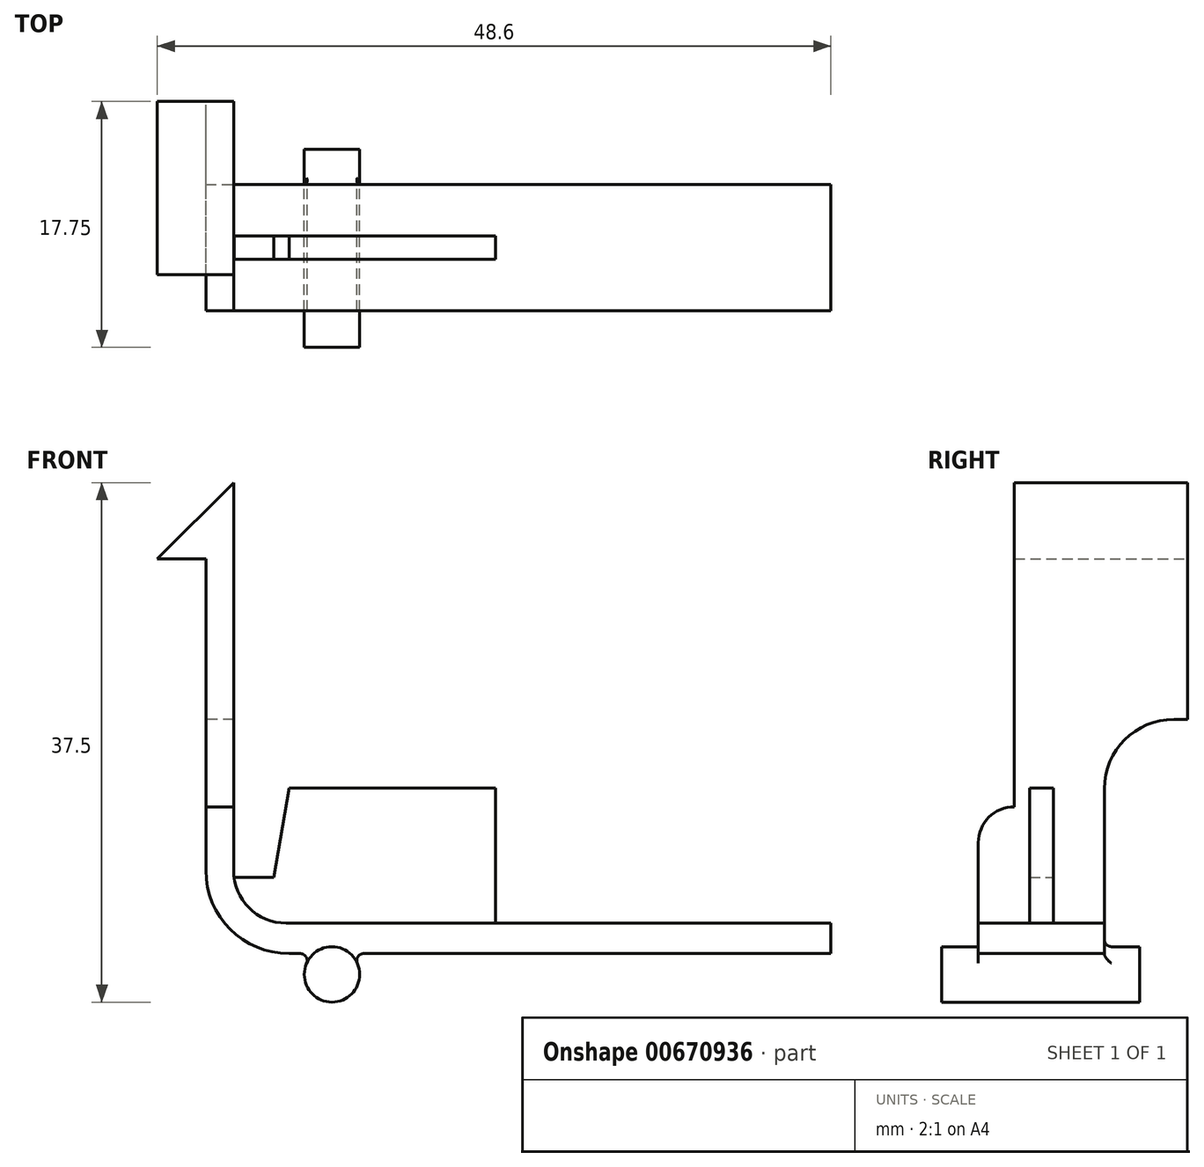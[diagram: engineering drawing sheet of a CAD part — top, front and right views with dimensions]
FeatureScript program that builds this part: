
annotation { "Feature Type Name" : "Feature", "Feature Type Description" : "" }
export const myFeature = defineFeature(function(context is Context, id is Id, definition is map)
    precondition{}
    {
        {
            var Q0;
            Q0=qCreatedBy(makeId("Front.planeOp"),FACE);
            var sketch = newSketch(context, id + "F0", { "sketchPlane" : qUnion([Q0])});
            skLineSegment(sketch, "E0", {"start": v(45.1, 3.5) * mm, "end": v(6, 3.5) * mm});
            skLineSegment(sketch, "E1", {"start": v(0, 9.5) * mm, "end": v(0, 32) * mm});
            skLineSegment(sketch, "E2", {"start": v(2, 37.5) * mm, "end": v(2, 9.5) * mm});
            skLineSegment(sketch, "E3", {"start": v(5.8, 5.7) * mm, "end": v(45.1, 5.7) * mm});
            skLineSegment(sketch, "E4", {"start": v(45.1, 3.5) * mm, "end": v(45.1, 5.7) * mm});
            skCircle(sketch, "E5", {"center": v(9.1, 2) * mm, "radius": 2 * mm});
            skPoint(sketch, "E6.visualSharp", {"position": v(0, 3.5) * mm});
            skArc(sketch, "E6.filletArc", {"start": v(0, 9.5) * mm, "mid": v(1.76, 5.26) * mm, "end": v(6, 3.5) * mm});
            skPoint(sketch, "E7.visualSharp", {"position": v(2, 5.7) * mm});
            skArc(sketch, "E7.filletArc", {"start": v(2, 9.5) * mm, "mid": v(3.11, 6.81) * mm, "end": v(5.8, 5.7) * mm});
            skLineSegment(sketch, "E8", {"start": v(2, 37.5) * mm, "end": v(-3.5, 32) * mm});
            skLineSegment(sketch, "E9", {"start": v(-3.5, 32) * mm, "end": v(0, 32) * mm});
            skSolve(sketch);
        }
        {
            var Q0;
            Q0=makeQuery(id+"F0.imprint","IMPRINT",FACE,{"disambiguationData":[TD([[makeQuery(id+"F0.imprint","IMPRINT",EDGE,{"derivedFrom":sQuery(id+"F0.wireOp",EDGE,"E1")}),-1.0]])]});
            extrude(context, id + "F1", {"entities" : qUnion([Q0]), "endBound" : BoundingType.SYMMETRIC, "depth" : 9.1 * mm, "offsetDistance" : 25 * mm});
        }
        {
            var Q0;
            {var subQ0=sQuery(id+"F0.wireOp",EDGE,"E5");var subQ1=sQuery(id+"F0.wireOp",EDGE,"E0");var subQ2=makeQuery(id+"F0.imprint","INTERSECT",VERTEX,{"disambiguationData":[OD(0.0)],"derivedFrom":[subQ1,subQ0]});Q0=makeQuery(id+"F0.imprint","IMPRINT",FACE,{"disambiguationData":[TD([[makeQuery(id+"F0.imprint","IMPRINT",EDGE,{"disambiguationData":[TD([[subQ2,-1.0]])],"derivedFrom":subQ1}),1.0]])]});}
            var Q1;
            {var subQ0=sQuery(id+"F0.wireOp",EDGE,"E5");var subQ1=sQuery(id+"F0.wireOp",EDGE,"E0");var subQ2=makeQuery(id+"F0.imprint","INTERSECT",VERTEX,{"disambiguationData":[OD(0.0)],"derivedFrom":[subQ1,subQ0]});Q1=makeQuery(id+"F0.imprint","IMPRINT",FACE,{"disambiguationData":[TD([[makeQuery(id+"F0.imprint","IMPRINT",EDGE,{"disambiguationData":[TD([[subQ2,-1.0]])],"derivedFrom":subQ1}),-1.0]])]});}
            extrude(context, id + "F2", {"entities" : qUnion([Q0, Q1]), "operationType" : NewBodyOperationType.ADD, "depth" : (2.6 + 9.2 / 2) * mm, "offsetDistance" : 25 * mm});
        }
        {
            var Q0;
            Q0=makeQuery(id+"F2.opExtrude","CAP_FACE",FACE,{"disambiguationData":[OSD([sQuery(id+"F0.wireOp",EDGE,"E5")])],"isStart":false});
            extrude(context, id + "F3", {"entities" : qUnion([Q0]), "operationType" : NewBodyOperationType.ADD, "oppositeDirection" : true, "depth" : 14.3 * mm, "offsetDistance" : 25 * mm});
        }
        {
            var Q0;
            Q0=qCreatedBy(makeId("Front.planeOp"),FACE);
            var sketch = newSketch(context, id + "F4", { "sketchPlane" : qUnion([Q0])});
            skLineSegment(sketch, "E10", {"start": v(20.9, 15.45) * mm, "end": v(6, 15.45) * mm});
            skLineSegment(sketch, "E11", {"start": v(6, 15.45) * mm, "end": v(4.9, 9) * mm});
            skLineSegment(sketch, "E12", {"start": v(4.9, 9) * mm, "end": v(2, 9) * mm});
            skLineSegment(sketch, "E13", {"start": v(20.9, 15.45) * mm, "end": v(20.9, 5.7) * mm});
            skArc(sketch, "E14.0", {"start": v(2.03, 9) * mm, "mid": v(3.3, 6.64) * mm, "end": v(5.8, 5.7) * mm});
            skLineSegment(sketch, "E15.0", {"start": v(5.8, 5.7) * mm, "end": v(20.9, 5.7) * mm});
            skPoint(sketch, "E16.orphan", {"position": v(2, 37.5) * mm});
            skPoint(sketch, "E17.orphan", {"position": v(45.1, 5.7) * mm});
            skPoint(sketch, "E18.orphan", {"position": v(2, 9.5) * mm});
            skSolve(sketch);
        }
        {
            var Q0;
            Q0 = qSketchRegion(id + "F4", true);
            extrude(context, id + "F5", {"entities" : qUnion([Q0]), "operationType" : NewBodyOperationType.ADD, "endBound" : BoundingType.SYMMETRIC, "depth" : 1.7 * mm, "offsetDistance" : 25 * mm});
        }
        {
            var Q0;
            Q0=makeQuery(id+"F1.opExtrude","CAP_FACE",FACE,{"disambiguationData":[OSD([sQuery(id+"F0.wireOp",EDGE,"E0"),sQuery(id+"F0.wireOp",EDGE,"E1"),sQuery(id+"F0.wireOp",EDGE,"E2"),sQuery(id+"F0.wireOp",EDGE,"E3"),sQuery(id+"F0.wireOp",EDGE,"E4"),sQuery(id+"F0.wireOp",EDGE,"E5"),sQuery(id+"F0.wireOp",EDGE,"E6.filletArc"),sQuery(id+"F0.wireOp",EDGE,"E7.filletArc"),sQuery(id+"F0.wireOp",EDGE,"E8"),sQuery(id+"F0.wireOp",EDGE,"E9")])],"isStart":true});
            var sketch = newSketch(context, id + "F6", { "sketchPlane" : qUnion([Q0])});
            skLineSegment(sketch, "E19.0.3", {"start": v(0, 15.4) * mm, "end": v(0, 32) * mm});
            skLineSegment(sketch, "E19.0.4", {"start": v(0, 32) * mm, "end": v(3.5, 32) * mm});
            skLineSegment(sketch, "E19.0.5", {"start": v(3.5, 32) * mm, "end": v(-2, 37.5) * mm});
            skLineSegment(sketch, "E19.0.6", {"start": v(-2, 37.5) * mm, "end": v(-2, 15.4) * mm});
            skLineSegment(sketch, "E20", {"start": v(0, 15.4) * mm, "end": v(-2, 15.4) * mm});
            skPoint(sketch, "E19.0.7.start.orphan", {"position": v(-2, 9.5) * mm});
            skPoint(sketch, "E19.0.2.end.orphan", {"position": v(0, 9.5) * mm});
            skPoint(sketch, "E19.0.8.start.orphan", {"position": v(-5.8, 5.7) * mm});
            skPoint(sketch, "E19.0.1.end.orphan", {"position": v(-6, 3.5) * mm});
            skPoint(sketch, "E19.0.0.end.orphan", {"position": v(-7.78, 3.5) * mm});
            skPoint(sketch, "E19.0.10.end.orphan", {"position": v(-10.42, 3.5) * mm});
            skPoint(sketch, "E19.0.9.end.orphan", {"position": v(-45.1, 3.5) * mm});
            skPoint(sketch, "E19.0.9.start.orphan", {"position": v(-45.1, 5.7) * mm});
            skSolve(sketch);
        }
        {
            var Q0;
            Q0 = qSketchRegion(id + "F6", true);
            extrude(context, id + "F7", {"entities" : qUnion([Q0]), "operationType" : NewBodyOperationType.ADD, "depth" : 6 * mm, "offsetDistance" : 25 * mm});
        }
        {
            var Q0;
            Q0=makeQuery(id+"F7.boolean.opBoolean","MERGE",FACE,{"derivedFrom":[makeQuery(id+"F1.opExtrude","SWEPT_FACE",FACE,{"disambiguationData":[OSD([sQuery(id+"F0.wireOp",EDGE,"E1")])]}),makeQuery(id+"F7.opExtrude","SWEPT_FACE",FACE,{"disambiguationData":[OSD([sQuery(id+"F6.wireOp",EDGE,"E19.0.3")])]})]});
            var sketch = newSketch(context, id + "F8", { "sketchPlane" : qUnion([Q0])});
            skLineSegment(sketch, "E21", {"start": v(-4.55, 37.5) * mm, "end": v(-4.55, 42.04) * mm});
            skLineSegment(sketch, "E22", {"start": v(-4.55, 42.04) * mm, "end": v(-13.48, 42.04) * mm});
            skLineSegment(sketch, "E23", {"start": v(-13.48, 42.04) * mm, "end": v(-13.48, 13.67) * mm});
            skLineSegment(sketch, "E24", {"start": v(-13.48, 13.67) * mm, "end": v(-4.55, 13.67) * mm});
            skLineSegment(sketch, "E25", {"start": v(-4.55, 13.67) * mm, "end": v(-4.55, 15.4) * mm});
            skLineSegment(sketch, "E26", {"start": v(-9.55, 20.4) * mm, "end": v(-10.55, 20.4) * mm});
            skLineSegment(sketch, "E27", {"start": v(-10.55, 20.4) * mm, "end": v(-10.55, 37.5) * mm});
            skLineSegment(sketch, "E28", {"start": v(-10.55, 37.5) * mm, "end": v(-4.55, 37.5) * mm});
            skPoint(sketch, "E29.visualSharp", {"position": v(-4.55, 20.4) * mm});
            skArc(sketch, "E29.filletArc", {"start": v(-4.55, 15.4) * mm, "mid": v(-6.01, 18.94) * mm, "end": v(-9.55, 20.4) * mm});
            skSolve(sketch);
        }
        {
            var Q0;
            Q0=makeQuery(id+"F8.imprint","IMPRINT",FACE,{"disambiguationData":[TD([[makeQuery(id+"F8.imprint","IMPRINT",EDGE,{"derivedFrom":sQuery(id+"F8.wireOp",EDGE,"E21")}),1.0]])]});
            var Q1;
            {var subQ0=sQuery(id+"F8.wireOp",EDGE,"E26");Q1=makeQuery(id+"F8.imprint","IMPRINT",FACE,{"disambiguationData":[TD([[makeQuery(id+"F8.imprint","IMPRINT",EDGE,{"derivedFrom":subQ0}),1.0]])]});}
            extrude(context, id + "F9", {"entities" : qUnion([Q0, Q1]), "operationType" : NewBodyOperationType.REMOVE, "oppositeDirection" : true, "depth" : 3.6 * mm, "offsetDistance" : 25 * mm});
        }
        {
            var Q0;
            Q0=makeQuery(id+"F7.boolean.opBoolean","MERGE",FACE,{"derivedFrom":[makeQuery(id+"F1.opExtrude","SWEPT_FACE",FACE,{"disambiguationData":[OSD([sQuery(id+"F0.wireOp",EDGE,"E1")])]}),makeQuery(id+"F7.opExtrude","SWEPT_FACE",FACE,{"disambiguationData":[OSD([sQuery(id+"F6.wireOp",EDGE,"E19.0.3")])]})]});
            var sketch = newSketch(context, id + "F10", { "sketchPlane" : qUnion([Q0])});
            skLineSegment(sketch, "E30", {"start": v(1.95, 37.5) * mm, "end": v(1.95, 14.1) * mm});
            skArc(sketch, "E31", {"start": v(4.55, 11.5) * mm, "mid": v(3.79, 13.34) * mm, "end": v(1.95, 14.1) * mm});
            skLineSegment(sketch, "E32", {"start": v(4.55, 37.5) * mm, "end": v(4.55, 11.5) * mm});
            skLineSegment(sketch, "E33", {"start": v(4.55, 37.5) * mm, "end": v(1.95, 37.5) * mm});
            skSolve(sketch);
        }
        {
            var Q0;
            Q0 = qSketchRegion(id + "F10", true);
            extrude(context, id + "F11", {"entities" : qUnion([Q0]), "operationType" : NewBodyOperationType.REMOVE, "endBound" : BoundingType.SYMMETRIC, "oppositeDirection" : true, "depth" : 25 * mm, "offsetDistance" : 25 * mm});
        }
        {
            var Q0;
            {var subQ0=sQuery(id+"F0.wireOp",EDGE,"E0");var subQ1=sQuery(id+"F0.wireOp",EDGE,"E5");var subQ2=makeQuery(id+"F0.imprint","INTERSECT",VERTEX,{"disambiguationData":[OD(1.0)],"derivedFrom":[subQ0,subQ1]});var subQ4=makeQuery(id+"F1.opExtrude","SWEPT_EDGE",EDGE,{"disambiguationData":[OSD([subQ0,subQ1]),TDD([subQ2])]});Q0=makeQuery(id+"F3.boolean.opBoolean","MERGE",EDGE,{"derivedFrom":[makeQuery(id+"F2.boolean.opBoolean","SPLIT",EDGE,{"disambiguationData":[topologyDisambiguationEdgeConnected([makeQuery(id+"F1.opExtrude","SWEPT_FACE",FACE,{"disambiguationData":[OSD([subQ1])]})])],"derivedFrom":subQ4}),makeQuery(id+"F2.boolean.opBoolean","SPLIT",EDGE,{"disambiguationData":[topologyDisambiguationEdgeConnected([makeQuery(id+"F2.opExtrude","SWEPT_FACE",FACE,{"disambiguationData":[OSD([subQ1])]})])],"derivedFrom":subQ4})]});}
            var Q1;
            {var subQ0=sQuery(id+"F0.wireOp",EDGE,"E0");var subQ1=sQuery(id+"F0.wireOp",EDGE,"E5");var subQ2=makeQuery(id+"F0.imprint","INTERSECT",VERTEX,{"disambiguationData":[OD(0.0)],"derivedFrom":[subQ0,subQ1]});var subQ4=makeQuery(id+"F1.opExtrude","SWEPT_EDGE",EDGE,{"disambiguationData":[OSD([subQ0,subQ1]),TDD([subQ2])]});Q1=makeQuery(id+"F3.boolean.opBoolean","MERGE",EDGE,{"derivedFrom":[makeQuery(id+"F2.boolean.opBoolean","SPLIT",EDGE,{"disambiguationData":[topologyDisambiguationEdgeConnected([makeQuery(id+"F1.opExtrude","SWEPT_FACE",FACE,{"disambiguationData":[OSD([subQ1])]})])],"derivedFrom":subQ4}),makeQuery(id+"F2.boolean.opBoolean","SPLIT",EDGE,{"disambiguationData":[topologyDisambiguationEdgeConnected([makeQuery(id+"F2.opExtrude","SWEPT_FACE",FACE,{"disambiguationData":[OSD([subQ1])]})])],"derivedFrom":subQ4})]});}
            var Q2;
            Q2=makeQuery(id+"F1.opExtrude","CAP_EDGE",EDGE,{"disambiguationData":[OSD([sQuery(id+"F0.wireOp",EDGE,"E5")])],"isStart":false});
            var Q3;
            Q3=makeQuery(id+"F1.opExtrude","CAP_EDGE",EDGE,{"disambiguationData":[OSD([sQuery(id+"F0.wireOp",EDGE,"E5")])],"isStart":true});
            fillet(context, id + "F12", {"entities" : qUnion([Q0, Q1, Q2, Q3]), "radius" : .5 * mm, "tangentPropagation" : true, "allowEdgeOverflow" : false});
        }
    });
